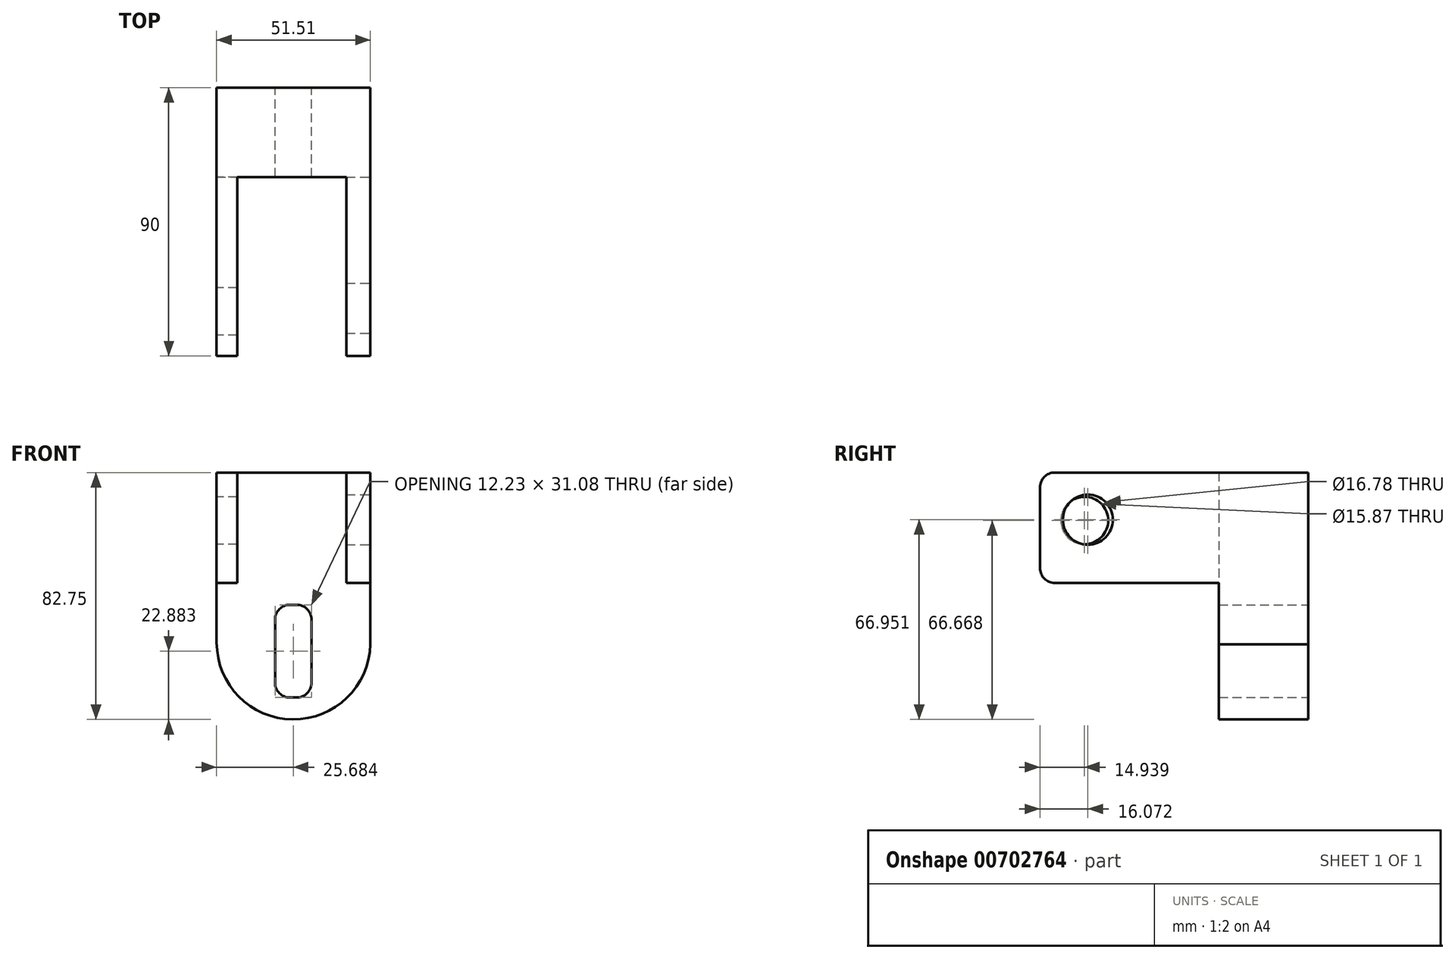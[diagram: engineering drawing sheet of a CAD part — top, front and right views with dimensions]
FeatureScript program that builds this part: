
annotation { "Feature Type Name" : "Feature", "Feature Type Description" : "" }
export const myFeature = defineFeature(function(context is Context, id is Id, definition is map)
    precondition{}
    {
        {
            var Q0;
            Q0=qCreatedBy(makeId("Front.planeOp"),FACE);
            var sketch = newSketch(context, id + "F0", { "sketchPlane" : qUnion([Q0])});
            skLineSegment(sketch, "E0", {"start": v(-31.8, 49.65) * mm, "end": v(19.71, 49.65) * mm});
            skLineSegment(sketch, "E1", {"start": v(19.71, 49.65) * mm, "end": v(19.71, -7.91) * mm});
            skPoint(sketch, "E2.start.orphan", {"position": v(-29.21, -7.91) * mm});
            skLineSegment(sketch, "E3", {"start": v(-31.8, 49.65) * mm, "end": v(-31.8, -7.34) * mm});
            skArc(sketch, "E4", {"start": v(-31.8, -7.34) * mm, "mid": v(-6.33, -33.1) * mm, "end": v(19.71, -7.91) * mm});
            skLineSegment(sketch, "E5.bottom", {"start": v(-7.23, 5.32) * mm, "end": v(-5, 5.32) * mm});
            skLineSegment(sketch, "E5.top", {"start": v(-7.23, -25.76) * mm, "end": v(-5, -25.76) * mm});
            skLineSegment(sketch, "E5.left", {"start": v(-12.23, 0.32) * mm, "end": v(-12.23, -20.76) * mm});
            skLineSegment(sketch, "E5.right", {"start": v(0, 0.32) * mm, "end": v(0, -20.76) * mm});
            skPoint(sketch, "E6.visualSharp", {"position": v(-12.23, 5.32) * mm});
            skArc(sketch, "E6.filletArc", {"start": v(-7.23, 5.32) * mm, "mid": v(-10.77, 3.86) * mm, "end": v(-12.23, 0.32) * mm});
            skPoint(sketch, "E7.visualSharp", {"position": v(0, 5.32) * mm});
            skArc(sketch, "E7.filletArc", {"start": v(0, 0.32) * mm, "mid": v(-1.46, 3.86) * mm, "end": v(-5, 5.32) * mm});
            skPoint(sketch, "E8.visualSharp", {"position": v(0, -25.76) * mm});
            skArc(sketch, "E8.filletArc", {"start": v(-5, -25.76) * mm, "mid": v(-1.46, -24.3) * mm, "end": v(0, -20.76) * mm});
            skPoint(sketch, "E9.visualSharp", {"position": v(-12.23, -25.76) * mm});
            skArc(sketch, "E9.filletArc", {"start": v(-12.23, -20.76) * mm, "mid": v(-10.77, -24.3) * mm, "end": v(-7.23, -25.76) * mm});
            skSolve(sketch);
        }
        {
            var Q0;
            Q0 = qSketchRegion(id + "F0", true);
            extrude(context, id + "F1", {"entities" : qUnion([Q0]), "depth" : 30 * mm, "offsetDistance" : 25 * mm});
        }
        {
            var Q0;
            Q0=makeQuery(id+"F1.opExtrude","CAP_FACE",FACE,{"disambiguationData":[OSD([sQuery(id+"F0.wireOp",EDGE,"E0"),sQuery(id+"F0.wireOp",EDGE,"E1"),sQuery(id+"F0.wireOp",EDGE,"E3"),sQuery(id+"F0.wireOp",EDGE,"E4"),sQuery(id+"F0.wireOp",EDGE,"E5.bottom"),sQuery(id+"F0.wireOp",EDGE,"E5.top"),sQuery(id+"F0.wireOp",EDGE,"E5.left"),sQuery(id+"F0.wireOp",EDGE,"E5.right"),sQuery(id+"F0.wireOp",EDGE,"E6.filletArc"),sQuery(id+"F0.wireOp",EDGE,"E7.filletArc"),sQuery(id+"F0.wireOp",EDGE,"E8.filletArc"),sQuery(id+"F0.wireOp",EDGE,"E9.filletArc")])],"isStart":false});
            var sketch = newSketch(context, id + "F2", { "sketchPlane" : qUnion([Q0])});
            skLineSegment(sketch, "E10", {"start": v(-31.8, 49.65) * mm, "end": v(-24.9, 49.65) * mm});
            skLineSegment(sketch, "E11", {"start": v(-24.9, 49.65) * mm, "end": v(-24.9, 12.65) * mm});
            skLineSegment(sketch, "E12", {"start": v(-24.9, 12.65) * mm, "end": v(-31.8, 12.65) * mm});
            skLineSegment(sketch, "E13", {"start": v(-31.8, 12.65) * mm, "end": v(-31.8, 49.65) * mm});
            skLineSegment(sketch, "E14", {"start": v(19.71, 49.65) * mm, "end": v(11.66, 49.65) * mm});
            skLineSegment(sketch, "E15", {"start": v(11.66, 49.65) * mm, "end": v(11.66, 12.65) * mm});
            skLineSegment(sketch, "E16", {"start": v(11.66, 12.65) * mm, "end": v(19.71, 12.65) * mm});
            skLineSegment(sketch, "E17", {"start": v(19.71, 12.65) * mm, "end": v(19.71, 49.65) * mm});
            skSolve(sketch);
        }
        {
            var Q0;
            Q0 = qSketchRegion(id + "F2", true);
            extrude(context, id + "F3", {"entities" : qUnion([Q0]), "operationType" : NewBodyOperationType.ADD, "depth" : 60 * mm, "offsetDistance" : 25 * mm});
        }
        {
            var Q0;
            Q0=makeQuery(id+"F3.opExtrude","CAP_EDGE",EDGE,{"disambiguationData":[OSD([sQuery(id+"F2.wireOp",EDGE,"E14")])],"isStart":false});
            var Q1;
            Q1=makeQuery(id+"F3.opExtrude","CAP_EDGE",EDGE,{"disambiguationData":[OSD([sQuery(id+"F2.wireOp",EDGE,"E16")])],"isStart":false});
            var Q2;
            Q2=makeQuery(id+"F3.opExtrude","CAP_EDGE",EDGE,{"disambiguationData":[OSD([sQuery(id+"F2.wireOp",EDGE,"E10")])],"isStart":false});
            var Q3;
            Q3=makeQuery(id+"F3.opExtrude","CAP_EDGE",EDGE,{"disambiguationData":[OSD([sQuery(id+"F2.wireOp",EDGE,"E12")])],"isStart":false});
            fillet(context, id + "F4", {"entities" : qUnion([Q0, Q1, Q2, Q3]), "radius" : 5 * mm, "tangentPropagation" : true, "allowEdgeOverflow" : false});
        }
        {
            var Q0;
            Q0=makeQuery(id+"F3.boolean.opBoolean","MERGE",FACE,{"derivedFrom":[makeQuery(id+"F1.opExtrude","SWEPT_FACE",FACE,{"disambiguationData":[OSD([sQuery(id+"F0.wireOp",EDGE,"E1")])]}),makeQuery(id+"F3.opExtrude","SWEPT_FACE",FACE,{"disambiguationData":[OSD([sQuery(id+"F2.wireOp",EDGE,"E17")])]})]});
            var sketch = newSketch(context, id + "F5", { "sketchPlane" : qUnion([Q0])});
            skCircle(sketch, "E18", {"center": v(-73.93, 33.85) * mm, "radius": 8.39 * mm});
            skSolve(sketch);
        }
        {
            var Q0;
            Q0 = qSketchRegion(id + "F5", true);
            extrude(context, id + "F6", {"entities" : qUnion([Q0]), "operationType" : NewBodyOperationType.REMOVE, "oppositeDirection" : true, "depth" : 30 * mm, "offsetDistance" : 25 * mm});
        }
        {
            var Q0;
            Q0=makeQuery(id+"F3.boolean.opBoolean","MERGE",FACE,{"derivedFrom":[makeQuery(id+"F1.opExtrude","SWEPT_FACE",FACE,{"disambiguationData":[OSD([sQuery(id+"F0.wireOp",EDGE,"E3")])]}),makeQuery(id+"F3.opExtrude","SWEPT_FACE",FACE,{"disambiguationData":[OSD([sQuery(id+"F2.wireOp",EDGE,"E13")])]})]});
            var sketch = newSketch(context, id + "F7", { "sketchPlane" : qUnion([Q0])});
            skCircle(sketch, "E19", {"center": v(75.06, 33.57) * mm, "radius": 7.94 * mm});
            skSolve(sketch);
        }
        {
            var Q0;
            Q0 = qSketchRegion(id + "F7", true);
            extrude(context, id + "F8", {"entities" : qUnion([Q0]), "operationType" : NewBodyOperationType.REMOVE, "oppositeDirection" : true, "depth" : 30 * mm, "offsetDistance" : 25 * mm});
        }
    });
